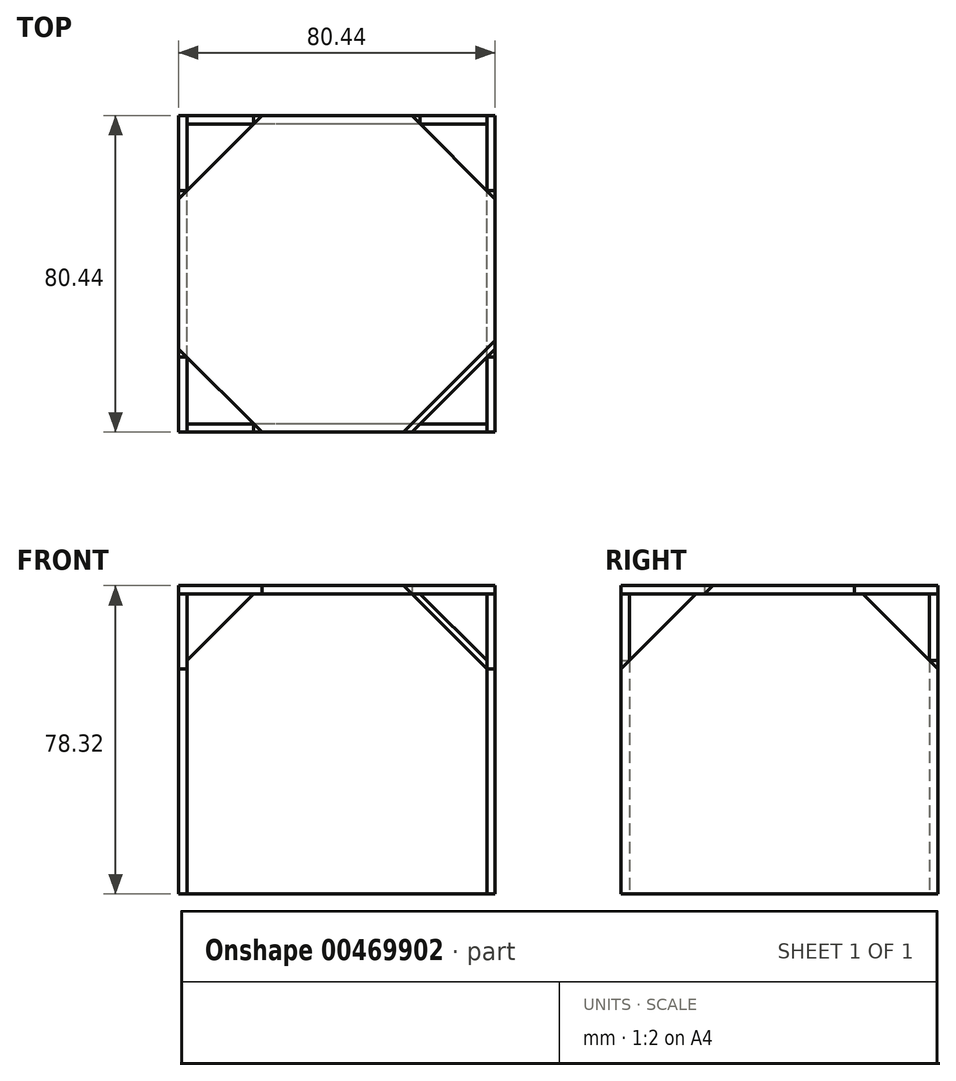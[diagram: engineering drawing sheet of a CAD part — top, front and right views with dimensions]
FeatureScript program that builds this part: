
annotation { "Feature Type Name" : "Feature", "Feature Type Description" : "" }
export const myFeature = defineFeature(function(context is Context, id is Id, definition is map)
    precondition{}
    {
        {
            var Q0;
            Q0=qCreatedBy(makeId("Front.planeOp"),FACE);
            var sketch = newSketch(context, id + "F0", { "sketchPlane" : qUnion([Q0])});
            skLineSegment(sketch, "E0.bottom", {"start": v(38.1, 38.1) * mm, "end": v(-38.1, 38.1) * mm});
            skLineSegment(sketch, "E0.top", {"start": v(38.1, -38.1) * mm, "end": v(-38.1, -38.1) * mm});
            skLineSegment(sketch, "E0.left", {"start": v(38.1, 38.1) * mm, "end": v(38.1, -38.1) * mm});
            skLineSegment(sketch, "E0.right", {"start": v(-38.1, 38.1) * mm, "end": v(-38.1, -38.1) * mm});
            skPoint(sketch, "E0.middle", {"position": v(0, 0) * mm});
            skLineSegment(sketch, "E1", {"start": v(-21.17, 38.1) * mm, "end": v(-38.1, 21.17) * mm});
            skLineSegment(sketch, "E2", {"start": v(21.17, 38.1) * mm, "end": v(38.1, 21.17) * mm});
            skLineSegment(sketch, "E3", {"start": v(38.1, -21.17) * mm, "end": v(21.17, -38.1) * mm});
            skLineSegment(sketch, "E4", {"start": v(-21.17, -38.1) * mm, "end": v(-38.1, -21.17) * mm});
            skSolve(sketch);
        }
        {
            var Q0;
            Q0=qCreatedBy(makeId("Right.planeOp"),FACE);
            var sketch = newSketch(context, id + "F1", { "sketchPlane" : qUnion([Q0])});
            skLineSegment(sketch, "E5.bottom", {"start": v(-40.22, 38.1) * mm, "end": v(40.22, 38.1) * mm});
            skLineSegment(sketch, "E5.top", {"start": v(-40.22, -38.1) * mm, "end": v(40.22, -38.1) * mm});
            skLineSegment(sketch, "E5.left", {"start": v(-40.22, 38.1) * mm, "end": v(-40.22, -38.1) * mm});
            skLineSegment(sketch, "E5.right", {"start": v(40.22, 38.1) * mm, "end": v(40.22, -38.1) * mm});
            skPoint(sketch, "E5.middle", {"position": v(0, 0) * mm});
            skLineSegment(sketch, "E6", {"start": v(-21.17, 38.1) * mm, "end": v(-40.22, 19.05) * mm});
            skLineSegment(sketch, "E7", {"start": v(40.22, 19.05) * mm, "end": v(21.17, 38.1) * mm});
            skLineSegment(sketch, "E8", {"start": v(40.22, -19.05) * mm, "end": v(21.17, -38.1) * mm});
            skLineSegment(sketch, "E9", {"start": v(-40.22, -19.05) * mm, "end": v(-21.17, -38.1) * mm});
            skSolve(sketch);
        }
        {
            var Q0;
            Q0=qCreatedBy(makeId("Top.planeOp"),FACE);
            var sketch = newSketch(context, id + "F2", { "sketchPlane" : qUnion([Q0])});
            skLineSegment(sketch, "E10.bottom", {"start": v(38.1, 38.1) * mm, "end": v(-38.1, 38.1) * mm});
            skLineSegment(sketch, "E10.top", {"start": v(38.1, -38.1) * mm, "end": v(-38.1, -38.1) * mm});
            skLineSegment(sketch, "E10.left", {"start": v(38.1, 38.1) * mm, "end": v(38.1, -38.1) * mm});
            skLineSegment(sketch, "E10.right", {"start": v(-38.1, 38.1) * mm, "end": v(-38.1, -38.1) * mm});
            skPoint(sketch, "E10.middle", {"position": v(0, 0) * mm});
            skLineSegment(sketch, "E11.bottom", {"start": v(40.22, 40.22) * mm, "end": v(-40.22, 40.22) * mm});
            skLineSegment(sketch, "E11.top", {"start": v(40.22, -40.22) * mm, "end": v(-40.22, -40.22) * mm});
            skLineSegment(sketch, "E11.left", {"start": v(40.22, 40.22) * mm, "end": v(40.22, -40.22) * mm});
            skLineSegment(sketch, "E11.right", {"start": v(-40.22, 40.22) * mm, "end": v(-40.22, -40.22) * mm});
            skLineSegment(sketch, "E12", {"start": v(-19.05, 40.22) * mm, "end": v(-40.22, 19.05) * mm});
            skLineSegment(sketch, "E13", {"start": v(19.05, 40.22) * mm, "end": v(40.22, 19.05) * mm});
            skLineSegment(sketch, "E14", {"start": v(40.22, -19.05) * mm, "end": v(19.05, -40.22) * mm});
            skLineSegment(sketch, "E15", {"start": v(-40.22, -19.05) * mm, "end": v(-19.05, -40.22) * mm});
            skSolve(sketch);
        }
        {
            var Q0;
            {var subQ0=sQuery(id+"F0.wireOp",EDGE,"E1");Q0=makeQuery(id+"F0.imprint","IMPRINT",FACE,{"disambiguationData":[TD([[makeQuery(id+"F0.imprint","IMPRINT",EDGE,{"derivedFrom":subQ0}),1.0]])]});}
            var Q1;
            {var subQ3=sQuery(id+"F0.wireOp",EDGE,"E4");Q1=makeQuery(id+"F0.imprint","IMPRINT",FACE,{"disambiguationData":[TD([[makeQuery(id+"F0.imprint","IMPRINT",EDGE,{"derivedFrom":subQ3}),1.0]])]});}
            var Q2;
            {var subQ3=sQuery(id+"F0.wireOp",EDGE,"E3");Q2=makeQuery(id+"F0.imprint","IMPRINT",FACE,{"disambiguationData":[TD([[makeQuery(id+"F0.imprint","IMPRINT",EDGE,{"derivedFrom":subQ3}),1.0]])]});}
            extrude(context, id + "F3", {"entities" : qUnion([Q0, Q1, Q2]), "depth" : 40.22 * mm, "hasSecondDirection" : true, "secondDirectionOppositeDirection" : false, "secondDirectionDepth" : 38.1 * mm});
        }
        {
            var Q0;
            {var subQ0=sQuery(id+"F0.wireOp",EDGE,"E1");Q0=makeQuery(id+"F0.imprint","IMPRINT",FACE,{"disambiguationData":[TD([[makeQuery(id+"F0.imprint","IMPRINT",EDGE,{"derivedFrom":subQ0}),1.0]])]});}
            var Q1;
            {var subQ3=sQuery(id+"F0.wireOp",EDGE,"E3");Q1=makeQuery(id+"F0.imprint","IMPRINT",FACE,{"disambiguationData":[TD([[makeQuery(id+"F0.imprint","IMPRINT",EDGE,{"derivedFrom":subQ3}),1.0]])]});}
            var Q2;
            {var subQ3=sQuery(id+"F0.wireOp",EDGE,"E4");Q2=makeQuery(id+"F0.imprint","IMPRINT",FACE,{"disambiguationData":[TD([[makeQuery(id+"F0.imprint","IMPRINT",EDGE,{"derivedFrom":subQ3}),1.0]])]});}
            extrude(context, id + "F4", {"entities" : qUnion([Q0, Q1, Q2]), "oppositeDirection" : true, "depth" : 40.22 * mm, "hasSecondDirection" : true, "secondDirectionOppositeDirection" : true, "secondDirectionDepth" : 38.1 * mm});
        }
        {
            var Q0;
            {var subQ3=sQuery(id+"F1.wireOp",EDGE,"E6");Q0=makeQuery(id+"F1.imprint","IMPRINT",FACE,{"disambiguationData":[TD([[makeQuery(id+"F1.imprint","IMPRINT",EDGE,{"derivedFrom":subQ3}),1.0]])]});}
            var Q1;
            {var subQ3=sQuery(id+"F1.wireOp",EDGE,"E9");Q1=makeQuery(id+"F1.imprint","IMPRINT",FACE,{"disambiguationData":[TD([[makeQuery(id+"F1.imprint","IMPRINT",EDGE,{"derivedFrom":subQ3}),-1.0]])]});}
            var Q2;
            {var subQ3=sQuery(id+"F1.wireOp",EDGE,"E8");Q2=makeQuery(id+"F1.imprint","IMPRINT",FACE,{"disambiguationData":[TD([[makeQuery(id+"F1.imprint","IMPRINT",EDGE,{"derivedFrom":subQ3}),1.0]])]});}
            extrude(context, id + "F5", {"entities" : qUnion([Q0, Q1, Q2]), "depth" : 40.22 * mm, "hasSecondDirection" : true, "secondDirectionOppositeDirection" : false, "secondDirectionDepth" : 38.1 * mm});
        }
        {
            var Q0;
            {var subQ3=sQuery(id+"F1.wireOp",EDGE,"E6");Q0=makeQuery(id+"F1.imprint","IMPRINT",FACE,{"disambiguationData":[TD([[makeQuery(id+"F1.imprint","IMPRINT",EDGE,{"derivedFrom":subQ3}),1.0]])]});}
            var Q1;
            {var subQ3=sQuery(id+"F1.wireOp",EDGE,"E8");Q1=makeQuery(id+"F1.imprint","IMPRINT",FACE,{"disambiguationData":[TD([[makeQuery(id+"F1.imprint","IMPRINT",EDGE,{"derivedFrom":subQ3}),1.0]])]});}
            var Q2;
            {var subQ3=sQuery(id+"F1.wireOp",EDGE,"E9");Q2=makeQuery(id+"F1.imprint","IMPRINT",FACE,{"disambiguationData":[TD([[makeQuery(id+"F1.imprint","IMPRINT",EDGE,{"derivedFrom":subQ3}),-1.0]])]});}
            extrude(context, id + "F6", {"entities" : qUnion([Q0, Q1, Q2]), "oppositeDirection" : true, "depth" : 40.22 * mm, "hasSecondDirection" : true, "secondDirectionOppositeDirection" : true, "secondDirectionDepth" : 38.1 * mm});
        }
        {
            var Q0;
            {var subQ0=sQuery(id+"F2.wireOp",EDGE,"E13");var subQ1=sQuery(id+"F2.wireOp",EDGE,"E10.left");var subQ2=makeQuery(id+"F2.imprint","INTERSECT",VERTEX,{"derivedFrom":[subQ1,subQ0]});Q0=makeQuery(id+"F2.imprint","IMPRINT",FACE,{"disambiguationData":[TD([[makeQuery(id+"F2.imprint","IMPRINT",EDGE,{"disambiguationData":[TD([[subQ2,-1.0]])],"derivedFrom":subQ1}),1.0]])]});}
            var Q1;
            {var subQ0=sQuery(id+"F2.wireOp",EDGE,"E13");var subQ1=sQuery(id+"F2.wireOp",EDGE,"E10.bottom");var subQ2=makeQuery(id+"F2.imprint","INTERSECT",VERTEX,{"derivedFrom":[subQ1,subQ0]});Q1=makeQuery(id+"F2.imprint","IMPRINT",FACE,{"disambiguationData":[TD([[makeQuery(id+"F2.imprint","IMPRINT",EDGE,{"disambiguationData":[TD([[subQ2,-1.0]])],"derivedFrom":subQ1}),-1.0]])]});}
            var Q2;
            {var subQ5=sQuery(id+"F2.wireOp",EDGE,"E13");var subQ13=sQuery(id+"F2.wireOp",EDGE,"E10.bottom");var subQ14=makeQuery(id+"F2.imprint","INTERSECT",VERTEX,{"derivedFrom":[subQ13,subQ5]});Q2=makeQuery(id+"F2.imprint","IMPRINT",FACE,{"disambiguationData":[TD([[makeQuery(id+"F2.imprint","IMPRINT",EDGE,{"disambiguationData":[TD([[subQ14,-1.0]])],"derivedFrom":subQ13}),1.0]])]});}
            var Q3;
            {var subQ0=sQuery(id+"F2.wireOp",EDGE,"E14");var subQ1=sQuery(id+"F2.wireOp",EDGE,"E10.top");var subQ2=makeQuery(id+"F2.imprint","INTERSECT",VERTEX,{"derivedFrom":[subQ1,subQ0]});Q3=makeQuery(id+"F2.imprint","IMPRINT",FACE,{"disambiguationData":[TD([[makeQuery(id+"F2.imprint","IMPRINT",EDGE,{"disambiguationData":[TD([[subQ2,-1.0]])],"derivedFrom":subQ1}),1.0]])]});}
            var Q4;
            {var subQ0=sQuery(id+"F2.wireOp",EDGE,"E12");var subQ1=sQuery(id+"F2.wireOp",EDGE,"E10.right");var subQ2=makeQuery(id+"F2.imprint","INTERSECT",VERTEX,{"derivedFrom":[subQ1,subQ0]});Q4=makeQuery(id+"F2.imprint","IMPRINT",FACE,{"disambiguationData":[TD([[makeQuery(id+"F2.imprint","IMPRINT",EDGE,{"disambiguationData":[TD([[subQ2,-1.0]])],"derivedFrom":subQ1}),-1.0]])]});}
            extrude(context, id + "F7", {"entities" : qUnion([Q0, Q1, Q2, Q3, Q4]), "depth" : 40.22 * mm, "hasSecondDirection" : true, "secondDirectionOppositeDirection" : false, "secondDirectionDepth" : 38.1 * mm});
        }
        {
            var Q0;
            Q0=makeQuery(id+"F3.opExtrude","CAP_VERTEX",VERTEX,{"disambiguationData":[OSD([sQuery(id+"F0.wireOp",EDGE,"E0.bottom"),sQuery(id+"F0.wireOp",EDGE,"E2")])],"isStart":true});
            var Q1;
            Q1=makeQuery(id+"F5.opExtrude","CAP_VERTEX",VERTEX,{"disambiguationData":[OSD([sQuery(id+"F1.wireOp",EDGE,"E5.bottom"),sQuery(id+"F1.wireOp",EDGE,"E6")])],"isStart":true});
            var Q2;
            Q2=makeQuery(id+"F3.opExtrude","CAP_VERTEX",VERTEX,{"disambiguationData":[OSD([sQuery(id+"F0.wireOp",EDGE,"E0.left"),sQuery(id+"F0.wireOp",EDGE,"E2")])],"isStart":true});
            cPlane(context, id + "F8", {"entities" : qUnion([Q0, Q1, Q2]), "cplaneType" : CPlaneType.THREE_POINT, "offset" : 25.4 * mm, "width" : 152.4 * mm, "height" : 152.4 * mm});
        }
        {
            var Q0;
            Q0=makeQuery(id+"F7.opExtrude","CAP_EDGE",EDGE,{"disambiguationData":[OSD([sQuery(id+"F2.wireOp",EDGE,"E14")])],"isStart":false});
            var Q1;
            Q1=makeQuery(id+"F3.opExtrude","CAP_EDGE",EDGE,{"disambiguationData":[OSD([sQuery(id+"F0.wireOp",EDGE,"E2")])],"isStart":false});
            chamfer(context, id + "F9", {"entities" : qUnion([Q0, Q1]), "chamferType" : ChamferType.OFFSET_ANGLE, "width" : 2.12 * mm, "oppositeDirection" : false, "angle" : 35.26 * degree, "tangentPropagation" : true});
        }
    });
